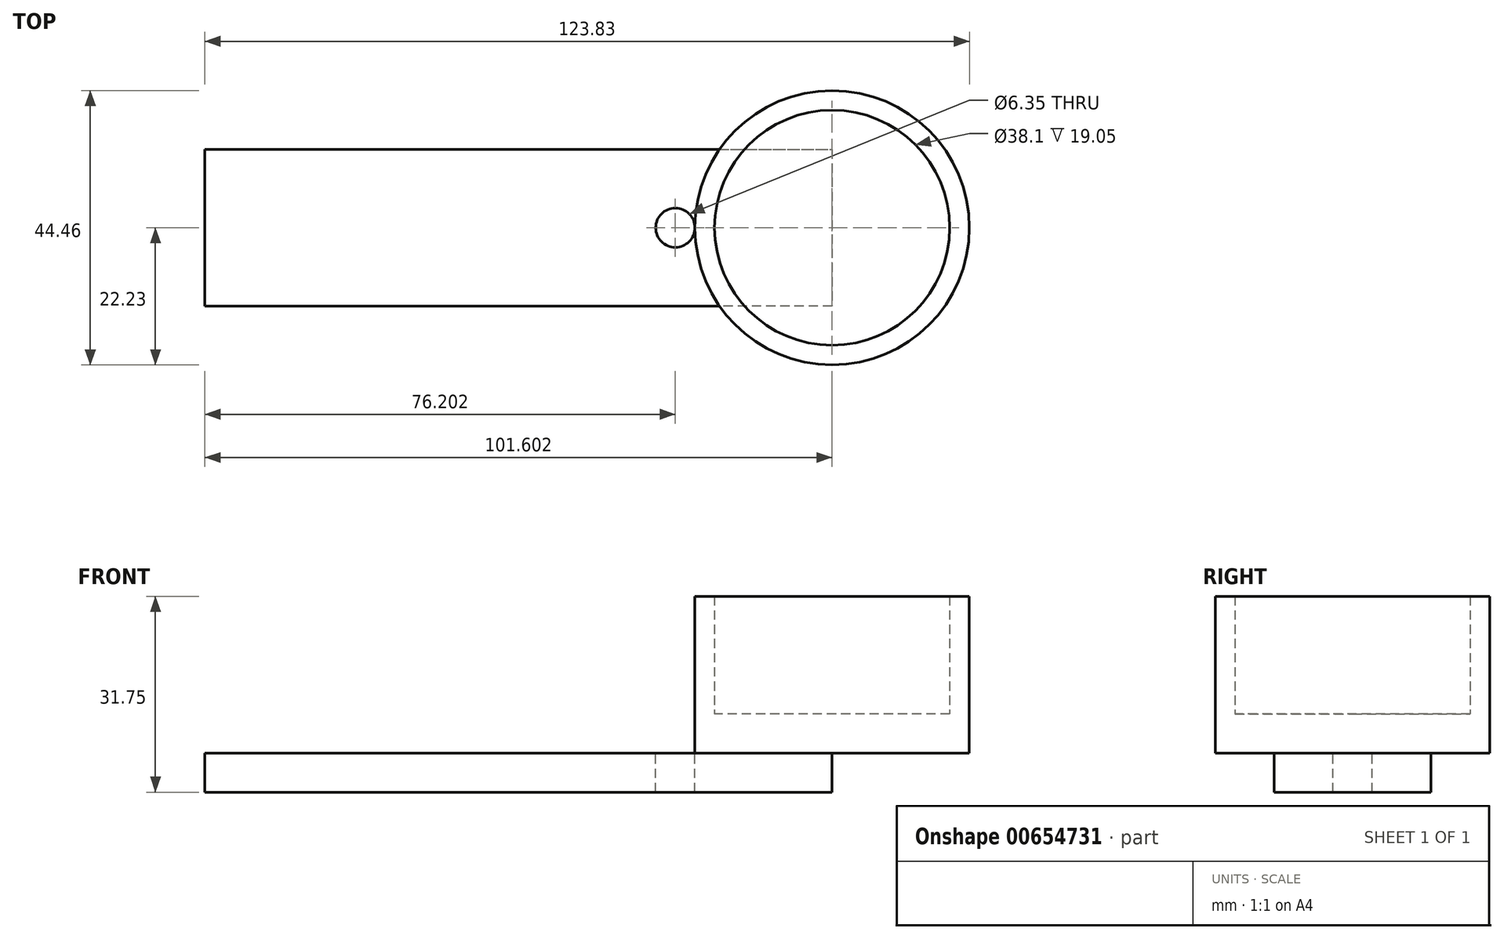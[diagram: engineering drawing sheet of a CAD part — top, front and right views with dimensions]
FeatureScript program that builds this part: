
annotation { "Feature Type Name" : "Feature", "Feature Type Description" : "" }
export const myFeature = defineFeature(function(context is Context, id is Id, definition is map)
    precondition{}
    {
        {
            var Q0;
            Q0=qCreatedBy(makeId("Top.planeOp"),FACE);
            var sketch = newSketch(context, id + "F0", { "sketchPlane" : qUnion([Q0])});
            skLineSegment(sketch, "E0", {"start": v(-42.87, 0) * mm, "end": v(-42.87, 12.7) * mm});
            skLineSegment(sketch, "E1", {"start": v(-42.87, 12.7) * mm, "end": v(58.73, 12.7) * mm});
            skLineSegment(sketch, "E2", {"start": v(58.73, 12.7) * mm, "end": v(58.73, -12.7) * mm});
            skLineSegment(sketch, "E3", {"start": v(58.73, -12.7) * mm, "end": v(-42.87, -12.7) * mm});
            skLineSegment(sketch, "E4", {"start": v(-42.87, -12.7) * mm, "end": v(-42.87, 0) * mm});
            skSolve(sketch);
        }
        {
            var Q0;
            Q0 = qSketchRegion(id + "F0", true);
            extrude(context, id + "F1", {"entities" : qUnion([Q0]), "depth" : 6.35 * mm, "offsetDistance" : 25.4 * mm});
        }
        {
            var Q0;
            Q0=makeQuery(id+"F1.opExtrude","CAP_FACE",FACE,{"disambiguationData":[OSD([sQuery(id+"F0.wireOp",EDGE,"E0"),sQuery(id+"F0.wireOp",EDGE,"E1"),sQuery(id+"F0.wireOp",EDGE,"E2"),sQuery(id+"F0.wireOp",EDGE,"E3"),sQuery(id+"F0.wireOp",EDGE,"E4")])],"isStart":false});
            var sketch = newSketch(context, id + "F2", { "sketchPlane" : qUnion([Q0])});
            skCircle(sketch, "E5", {"center": v(33.33, 0) * mm, "radius": 3.18 * mm});
            skSolve(sketch);
        }
        {
            var Q0;
            Q0=makeQuery(id+"F2.imprint","IMPRINT",FACE,{"disambiguationData":[TD([[makeQuery(id+"F2.imprint","IMPRINT",EDGE,{"derivedFrom":sQuery(id+"F2.wireOp",EDGE,"E5")}),1.0]])]});
            extrude(context, id + "F3", {"entities" : qUnion([Q0]), "operationType" : NewBodyOperationType.REMOVE, "oppositeDirection" : true, "depth" : 6.35 * mm, "offsetDistance" : 25.4 * mm});
        }
        {
            var Q0;
            Q0=makeQuery(id+"F1.opExtrude","CAP_FACE",FACE,{"disambiguationData":[OSD([sQuery(id+"F0.wireOp",EDGE,"E0"),sQuery(id+"F0.wireOp",EDGE,"E1"),sQuery(id+"F0.wireOp",EDGE,"E2"),sQuery(id+"F0.wireOp",EDGE,"E3"),sQuery(id+"F0.wireOp",EDGE,"E4")])],"isStart":false});
            var sketch = newSketch(context, id + "F4", { "sketchPlane" : qUnion([Q0])});
            skCircle(sketch, "E6", {"center": v(58.73, 0) * mm, "radius": 22.23 * mm});
            skCircle(sketch, "E7", {"center": v(58.73, 0) * mm, "radius": 19.05 * mm});
            skSolve(sketch);
        }
        {
            var Q0;
            {var subQ5=makeQuery(id+"F1.opExtrude","CAP_EDGE",EDGE,{"disambiguationData":[OSD([sQuery(id+"F0.wireOp",EDGE,"E2")])],"isStart":false});Q0=makeQuery(id+"F4.imprint","IMPRINT",FACE,{"disambiguationData":[TD([[makeQuery(id+"F4.imprint","IMPRINT",EDGE,{"derivedFrom":subQ5}),-1.0]])]});}
            var Q1;
            {var subQ5=makeQuery(id+"F1.opExtrude","CAP_EDGE",EDGE,{"disambiguationData":[OSD([sQuery(id+"F0.wireOp",EDGE,"E2")])],"isStart":false});Q1=makeQuery(id+"F4.imprint","IMPRINT",FACE,{"disambiguationData":[TD([[makeQuery(id+"F4.imprint","IMPRINT",EDGE,{"derivedFrom":subQ5}),1.0]])]});}
            extrude(context, id + "F5", {"entities" : qUnion([Q0, Q1]), "operationType" : NewBodyOperationType.ADD, "depth" : 6.35 * mm, "offsetDistance" : 25.4 * mm});
        }
        {
            var Q0;
            Q0 = qSketchRegion(id + "F4", true);
            extrude(context, id + "F6", {"entities" : qUnion([Q0]), "operationType" : NewBodyOperationType.ADD, "depth" : 25.4 * mm, "offsetDistance" : 25.4 * mm});
        }
    });
